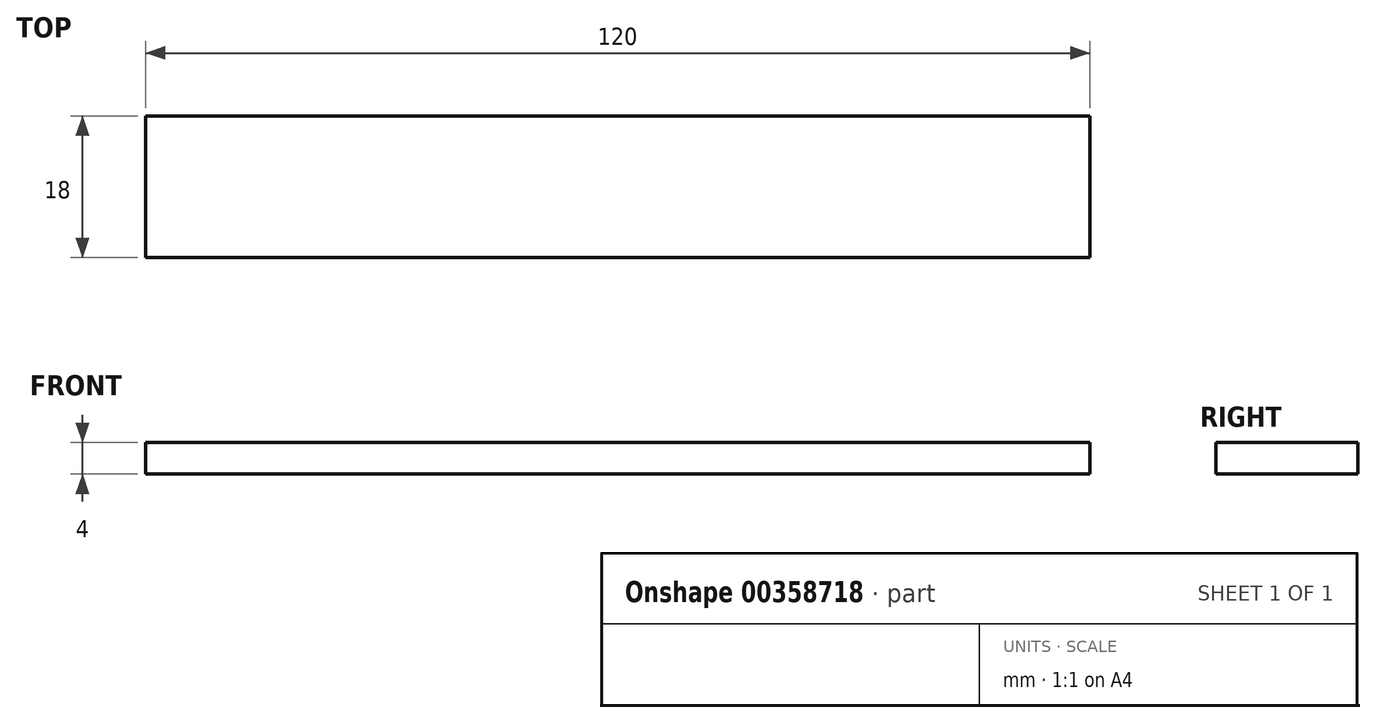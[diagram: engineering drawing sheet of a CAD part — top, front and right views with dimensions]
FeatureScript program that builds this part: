
annotation { "Feature Type Name" : "Feature", "Feature Type Description" : "" }
export const myFeature = defineFeature(function(context is Context, id is Id, definition is map)
    precondition{}
    {
        {
            var Q0;
            Q0=qCreatedBy(makeId("Right.planeOp"),FACE);
            var sketch = newSketch(context, id + "F0", { "sketchPlane" : qUnion([Q0])});
            skLineSegment(sketch, "E0.bottom", {"start": v(9, -2) * mm, "end": v(-9, -2) * mm});
            skLineSegment(sketch, "E0.top", {"start": v(9, 2) * mm, "end": v(-9, 2) * mm});
            skLineSegment(sketch, "E0.left", {"start": v(9, -2) * mm, "end": v(9, 2) * mm});
            skLineSegment(sketch, "E0.right", {"start": v(-9, -2) * mm, "end": v(-9, 2) * mm});
            skPoint(sketch, "E0.middle", {"position": v(0, 0) * mm});
            skSolve(sketch);
        }
        {
            var Q0;
            Q0=qSketchRegion(id+"F0",true);
            extrude(context, id + "F1", {"entities" : qUnion([Q0]), "depth" : 120 * mm});
        }
    });
